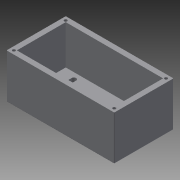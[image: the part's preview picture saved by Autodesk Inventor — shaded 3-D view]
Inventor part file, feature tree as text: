
AUTODESK INVENTOR PART (.ipt)
format: ipt  version: 2015 (Build 190159000, 159)  size: 151,040 bytes
history: native  units: mm
features: extrude x3, sketch x3, shell x1, fillet x1
ambient origin geometry x8: Origin, YZ Plane, XZ Plane, XY Plane, X Axis, Y Axis, Z Axis, Center Point
bodies: Solid1 (feature_tree)
feature tree (8):
  extrude  "Extrusion1"  Depth=40.0mm
  shell  "Shell2"  Thickness=30.0mm
  extrude  "Extrusion4"  Depth=3.5mm
  fillet  "Fillet1"  Radius=2.5mm
  extrude  "Extrusion5"  Depth=4.0mm TaperAngle=0.0deg
  sketch  "Sketch1"  dims[d0=72.8mm d1=40.0mm d2=30.0mm d3=0.0mm]
  sketch  "Sketch4"  dims[d23=3.5mm d26=2.0mm d27=2.5mm]
  sketch  "Sketch5"  dims[d28=2.5mm d29=4.0mm d30=0.0mm d31=0.4mm d32=19.0mm d33=19.0mm d34=5.0mm d35=3.0mm d36=5.0mm d37=3.0mm d38=5.0mm d39=3.0mm d40=5.0mm d41=3.0mm d42=17.2mm d43=17.2mm d44=6.0mm d45=12.0mm d46=6.0mm d47=12.0mm d48=10.0mm d49=0.0mm d52=20.0mm d53=20.0mm]
